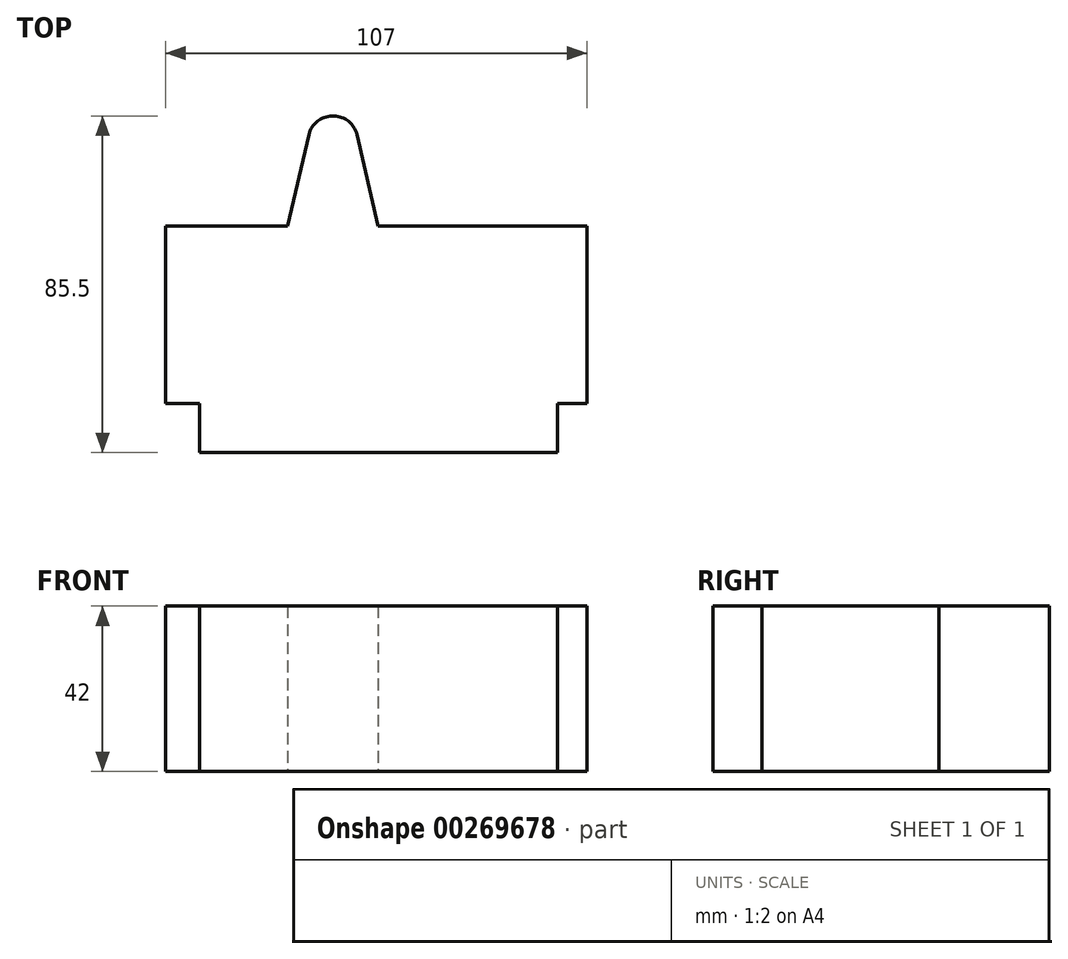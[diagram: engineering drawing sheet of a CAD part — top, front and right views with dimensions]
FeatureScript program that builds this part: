
annotation { "Feature Type Name" : "Feature", "Feature Type Description" : "" }
export const myFeature = defineFeature(function(context is Context, id is Id, definition is map)
    precondition{}
    {
        {
            var Q0;
            Q0=qCreatedBy(makeId("Top.planeOp"),FACE);
            var sketch = newSketch(context, id + "F0", { "sketchPlane" : qUnion([Q0])});
            skLineSegment(sketch, "E0.bottom", {"start": v(-26.28, 0) * mm, "end": v(80.72, 0) * mm});
            skLineSegment(sketch, "E0.top", {"start": v(-26.28, 45) * mm, "end": v(80.72, 45) * mm});
            skLineSegment(sketch, "E0.left", {"start": v(-26.28, 0) * mm, "end": v(-26.28, 45) * mm});
            skLineSegment(sketch, "E0.right", {"start": v(80.72, 0) * mm, "end": v(80.72, 45) * mm});
            skLineSegment(sketch, "E1.bottom", {"start": v(-17.68, 0) * mm, "end": v(73.32, 0) * mm});
            skLineSegment(sketch, "E1.top", {"start": v(-17.68, -12.5) * mm, "end": v(73.32, -12.5) * mm});
            skLineSegment(sketch, "E1.left", {"start": v(-17.68, 0) * mm, "end": v(-17.68, -12.5) * mm});
            skLineSegment(sketch, "E1.right", {"start": v(73.32, 0) * mm, "end": v(73.32, -12.5) * mm});
            skLineSegment(sketch, "E2", {"start": v(4.72, 45) * mm, "end": v(11.22, 73) * mm});
            skLineSegment(sketch, "E3", {"start": v(11.22, 73) * mm, "end": v(21.22, 73) * mm});
            skLineSegment(sketch, "E4", {"start": v(21.22, 73) * mm, "end": v(27.72, 45) * mm});
            skSolve(sketch);
        }
        {
            var Q0;
            Q0 = qSketchRegion(id + "F0", true);
            extrude(context, id + "F1", {"entities" : qUnion([Q0]), "depth" : 42 * mm});
        }
        {
            var Q0;
            Q0=makeQuery(id+"F1.opExtrude","SWEPT_EDGE",EDGE,{"disambiguationData":[OSD([sQuery(id+"F0.wireOp",EDGE,"E2"),sQuery(id+"F0.wireOp",EDGE,"E3")])]});
            var Q1;
            Q1=makeQuery(id+"F1.opExtrude","SWEPT_EDGE",EDGE,{"disambiguationData":[OSD([sQuery(id+"F0.wireOp",EDGE,"E3"),sQuery(id+"F0.wireOp",EDGE,"E4")])]});
            fillet(context, id + "F2", {"entities" : qUnion([Q0, Q1]), "radius" : 6 * mm, "tangentPropagation" : true, "allowEdgeOverflow" : false});
        }
    });
